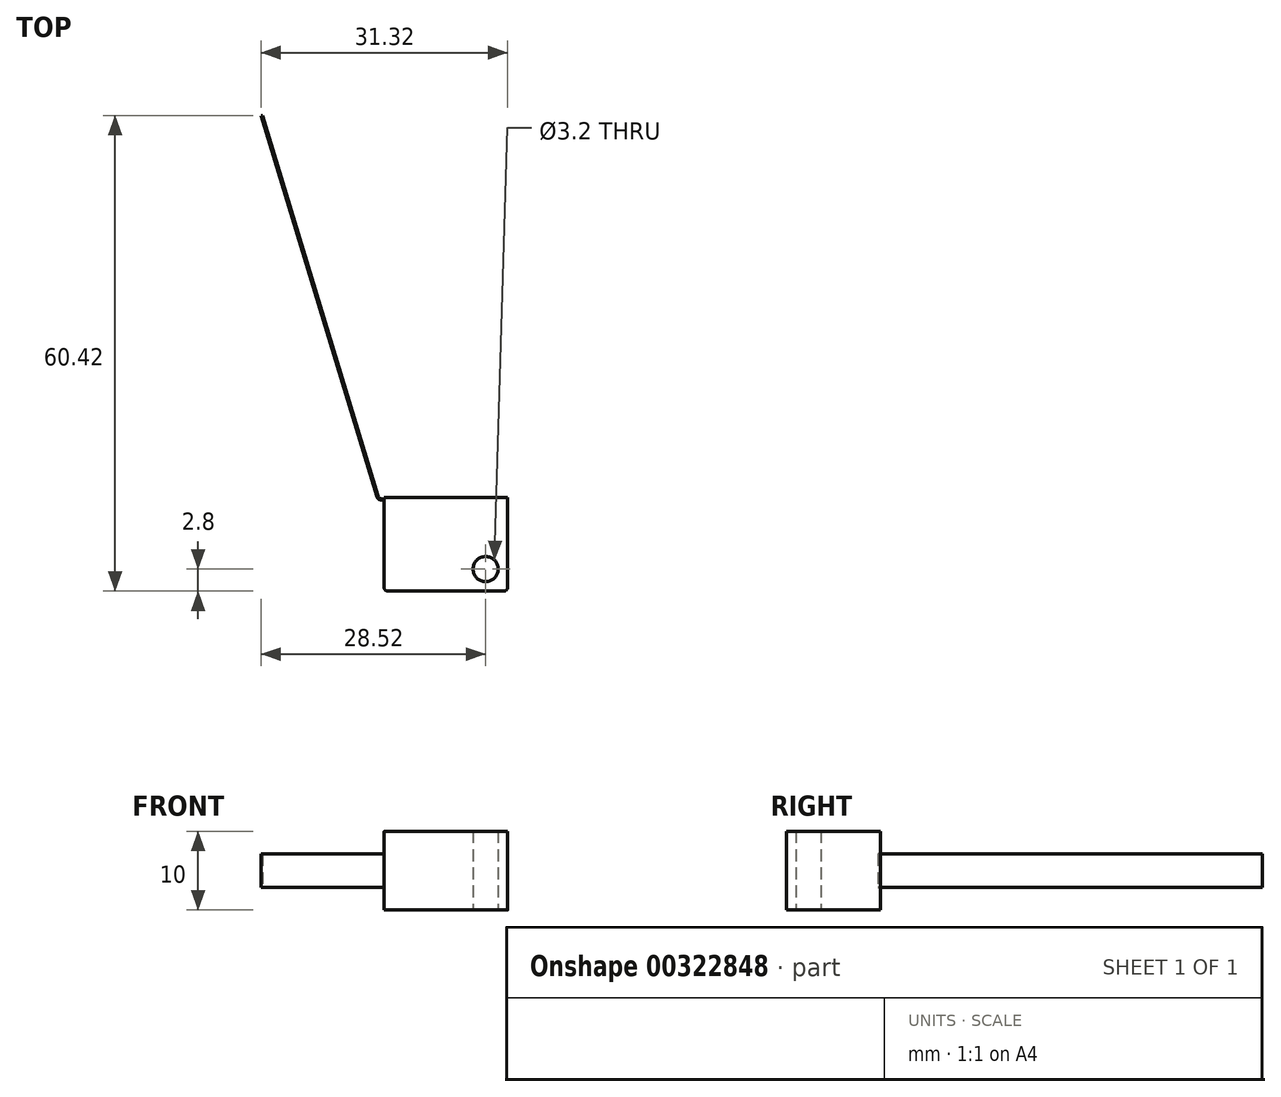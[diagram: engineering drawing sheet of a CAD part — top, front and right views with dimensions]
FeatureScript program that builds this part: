
annotation { "Feature Type Name" : "Feature", "Feature Type Description" : "" }
export const myFeature = defineFeature(function(context is Context, id is Id, definition is map)
    precondition{}
    {
        {
            var Q0;
            Q0=qCreatedBy(makeId("Top.planeOp"),FACE);
            var sketch = newSketch(context, id + "F0", { "sketchPlane" : qUnion([Q0])});
            skLineSegment(sketch, "E0.bottom", {"start": v(-7.85, 13.95) * mm, "end": v(7.35, 13.95) * mm});
            skLineSegment(sketch, "E0.top", {"start": v(-7.35, -13.95) * mm, "end": v(7.35, -13.95) * mm});
            skLineSegment(sketch, "E0.left", {"start": v(-7.85, 13.45) * mm, "end": v(-7.85, -13.45) * mm});
            skLineSegment(sketch, "E0.right", {"start": v(7.85, 13.45) * mm, "end": v(7.85, -13.45) * mm});
            skPoint(sketch, "E0.middle", {"position": v(0, 0) * mm});
            skLineSegment(sketch, "E1", {"start": v(-7.35, 13.95) * mm, "end": v(-5.05, 13.95) * mm});
            skCircle(sketch, "E2", {"center": v(-5.05, 11.15) * mm, "radius": 1.6 * mm});
            skPoint(sketch, "E3.visualSharp", {"position": v(-7.85, 13.95) * mm});
            skArc(sketch, "E3.filletArc", {"start": v(-7.35, 13.95) * mm, "mid": v(-7.7, 13.8) * mm, "end": v(-7.85, 13.45) * mm});
            skPoint(sketch, "E4.visualSharp", {"position": v(7.85, 13.95) * mm});
            skArc(sketch, "E4.filletArc", {"start": v(7.85, 13.45) * mm, "mid": v(7.7, 13.8) * mm, "end": v(7.35, 13.95) * mm});
            skPoint(sketch, "E5.visualSharp", {"position": v(-7.85, -13.95) * mm});
            skArc(sketch, "E5.filletArc", {"start": v(-7.85, -13.45) * mm, "mid": v(-7.7, -13.8) * mm, "end": v(-7.35, -13.95) * mm});
            skPoint(sketch, "E6.visualSharp", {"position": v(7.85, -13.95) * mm});
            skArc(sketch, "E6.filletArc", {"start": v(7.35, -13.95) * mm, "mid": v(7.7, -13.8) * mm, "end": v(7.85, -13.45) * mm});
            skLineSegment(sketch, "E7.bottom", {"start": v(7.85, -13.95) * mm, "end": v(5.05, -13.95) * mm});
            skLineSegment(sketch, "E7.left", {"start": v(7.85, -13.95) * mm, "end": v(7.85, -11.15) * mm});
            skCircle(sketch, "E8", {"center": v(5.05, -11.15) * mm, "radius": 1.6 * mm});
            skLineSegment(sketch, "E9", {"start": v(-7.85, 13.95) * mm, "end": v(-7.85, -2.05) * mm});
            skLineSegment(sketch, "E10", {"start": v(-7.85, -2.05) * mm, "end": v(7.85, -2.05) * mm});
            skLineSegment(sketch, "E11", {"start": v(7.85, -2.05) * mm, "end": v(-7.85, -2.05) * mm});
            skSolve(sketch);
        }
        {
            var Q0;
            {var subQ5=sQuery(id+"F0.wireOp",EDGE,"E1");Q0=makeQuery(id+"F0.imprint","IMPRINT",FACE,{"disambiguationData":[TD([[makeQuery(id+"F0.imprint","IMPRINT",EDGE,{"derivedFrom":subQ5}),-1.0]])]});}
            var Q1;
            {var subQ4=sQuery(id+"F0.wireOp",EDGE,"E0.top");Q1=makeQuery(id+"F0.imprint","IMPRINT",FACE,{"disambiguationData":[TD([[makeQuery(id+"F0.imprint","IMPRINT",EDGE,{"derivedFrom":subQ4}),1.0]])]});}
            extrude(context, id + "F1", {"entities" : qUnion([Q0, Q1]), "depth" : 10 * mm});
        }
        {
            var Q0;
            {var subQ4=sQuery(id+"F0.wireOp",EDGE,"E0.top");Q0=makeQuery(id+"F0.imprint","IMPRINT",FACE,{"disambiguationData":[TD([[makeQuery(id+"F0.imprint","IMPRINT",EDGE,{"derivedFrom":subQ4}),1.0]])]});}
            cPlane(context, id + "F2", {"entities" : qUnion([Q0]), "cplaneType" : CPlaneType.OFFSET, "offset" : 2.9 * mm, "width" : 150 * mm, "height" : 150 * mm});
        }
        {
            var Q0;
            Q0=qCreatedBy(id+"F2.planeOp",FACE);
            var sketch = newSketch(context, id + "F3", { "sketchPlane" : qUnion([Q0])});
            skLineSegment(sketch, "E12", {"start": v(-7.78, -2.22) * mm, "end": v(-8.16, -2.22) * mm});
            skLineSegment(sketch, "E13", {"start": v(-8.75, -2) * mm, "end": v(-23.47, 46.47) * mm});
            skLineSegment(sketch, "E14", {"start": v(-23.47, 46.47) * mm, "end": v(-8.75, -2) * mm});
            skLineSegment(sketch, "E15", {"start": v(-8.64, -1.86) * mm, "end": v(-23.32, 46.47) * mm});
            skLineSegment(sketch, "E16", {"start": v(-23.47, 46.47) * mm, "end": v(-23.32, 46.47) * mm});
            skLineSegment(sketch, "E17", {"start": v(-8.27, -2.36) * mm, "end": v(-7.78, -2.36) * mm});
            skLineSegment(sketch, "E18", {"start": v(-7.78, -2.36) * mm, "end": v(-7.78, -2.22) * mm});
            skPoint(sketch, "E19.visualSharp", {"position": v(-8.53, -2.22) * mm});
            skArc(sketch, "E19.filletArc", {"start": v(-8.64, -1.86) * mm, "mid": v(-8.46, -2.12) * mm, "end": v(-8.16, -2.22) * mm});
            skPoint(sketch, "E20.visualSharp", {"position": v(-8.53, -2.72) * mm});
            skPoint(sketch, "E21.visualSharp", {"position": v(-8.64, -2.36) * mm});
            skArc(sketch, "E21.filletArc", {"start": v(-8.75, -2) * mm, "mid": v(-8.57, -2.26) * mm, "end": v(-8.27, -2.36) * mm});
            skArc(sketch, "E22", {"start": v(-7.78, -1.22) * mm, "mid": v(-8.35, -1.52) * mm, "end": v(-7.78, -1.83) * mm});
            skLineSegment(sketch, "E23", {"start": v(-7.78, -1.83) * mm, "end": v(-7.78, -1.22) * mm});
            skSolve(sketch);
        }
        {
            var Q0;
            Q0=qSketchRegion(id+"F3",true);
            extrude(context, id + "F4", {"entities" : qUnion([Q0]), "depth" : 4.2 * mm});
        }
        {
            var Q0;
            Q0=makeQuery(id+"F4.opExtrude","SWEPT_BODY",BODY,{"disambiguationData":[OSD([sQuery(id+"F3.wireOp",EDGE,"E22"),sQuery(id+"F3.wireOp",EDGE,"E23")])]});
            deleteBodies(context, id + "F5", {"entities" : qUnion([Q0])});
        }
    });
